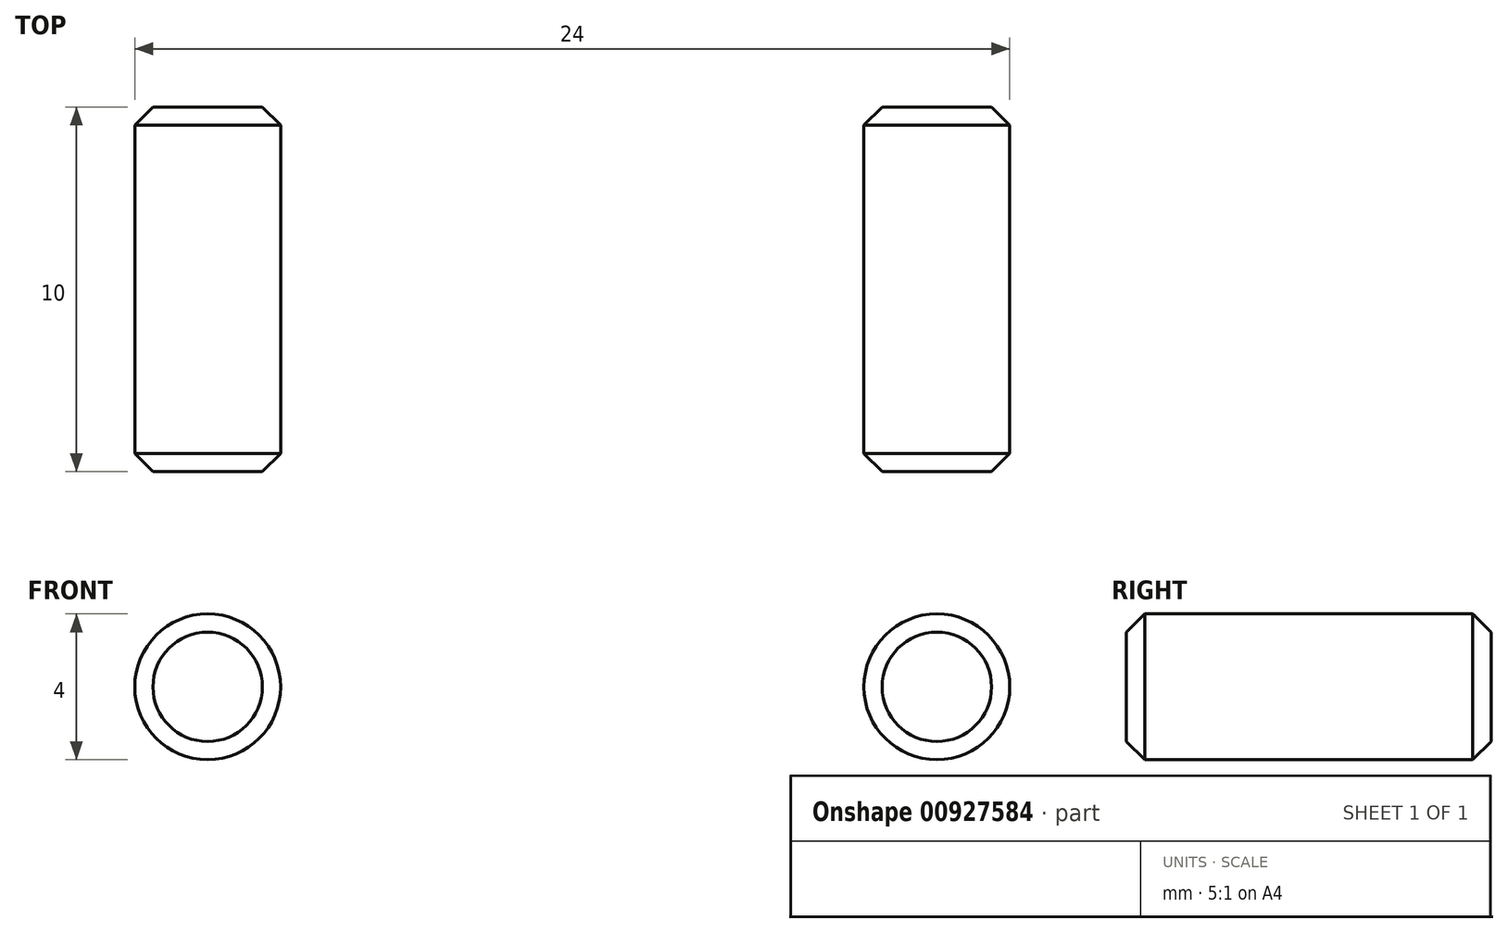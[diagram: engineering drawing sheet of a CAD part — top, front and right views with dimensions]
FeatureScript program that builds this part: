
annotation { "Feature Type Name" : "Feature", "Feature Type Description" : "" }
export const myFeature = defineFeature(function(context is Context, id is Id, definition is map)
    precondition{}
    {
        {
            var Q0;
            Q0=qCreatedBy(makeId("Right.planeOp"),FACE);
            var sketch = newSketch(context, id + "F0", { "sketchPlane" : qUnion([Q0])});
            skLineSegment(sketch, "E0.bottom", {"start": v(0, 0) * mm, "end": v(10, 0) * mm});
            skLineSegment(sketch, "E0.top", {"start": v(0, 11) * mm, "end": v(10, 11) * mm});
            skLineSegment(sketch, "E0.left", {"start": v(0, 0) * mm, "end": v(0, 11) * mm});
            skLineSegment(sketch, "E0.right", {"start": v(10, 0) * mm, "end": v(10, 11) * mm});
            skSolve(sketch);
        }
        {
            var Q0;
            Q0 = qSketchRegion(id + "F0", true);
            extrude(context, id + "F1", {"entities" : qUnion([Q0]), "oppositeDirection" : true, "depth" : 300 * mm, "offsetDistance" : 25 * mm});
        }
        {
            var Q0;
            Q0=makeQuery(id+"F1.opExtrude","SWEPT_FACE",FACE,{"disambiguationData":[OSD([sQuery(id+"F0.wireOp",EDGE,"E0.left")])]});
            var sketch = newSketch(context, id + "F2", { "sketchPlane" : qUnion([Q0])});
            skLineSegment(sketch, "E1", {"start": v(-271.81, 8) * mm, "end": v(-24.71, 8) * mm, "construction": true});
            skLineSegment(sketch, "E2.0", {"start": v(-327.74, 6.5) * mm, "end": v(9.8, 6.5) * mm, "construction": true});
            skLineSegment(sketch, "E3", {"start": v(-20, 30.82) * mm, "end": v(-20, -13.65) * mm, "construction": true});
            skLineSegment(sketch, "E4", {"start": v(-22.36, 15.05) * mm, "end": v(-22.36, 4.54) * mm, "construction": true});
            skLineSegment(sketch, "E5", {"start": v(-24.71, 15.08) * mm, "end": v(-24.71, 4.94) * mm, "construction": true});
            skLineSegment(sketch, "E6", {"start": v(-22.86, 11) * mm, "end": v(-22.36, 11) * mm});
            skLineSegment(sketch, "E7.MirrorCS", {"start": v(-21.86, 11) * mm, "end": v(-22.36, 11) * mm});
            skLineSegment(sketch, "E8", {"start": v(-24.71, 8) * mm, "end": v(-24.21, 8) * mm});
            skLineSegment(sketch, "E9", {"start": v(-24.21, 8) * mm, "end": v(-22.86, 11) * mm});
            skLineSegment(sketch, "E10", {"start": v(-20.5, 8) * mm, "end": v(-20, 8) * mm});
            skLineSegment(sketch, "E11", {"start": v(-21.86, 11) * mm, "end": v(-20.5, 8) * mm});
            skLineSegment(sketch, "E12.1.0.0", {"start": v(-25.21, 8) * mm, "end": v(-24.71, 8) * mm});
            skLineSegment(sketch, "E12.1.0.1", {"start": v(-26.57, 11) * mm, "end": v(-25.21, 8) * mm});
            skLineSegment(sketch, "E12.1.0.2", {"start": v(-26.57, 11) * mm, "end": v(-27.07, 11) * mm});
            skLineSegment(sketch, "E12.1.0.3", {"start": v(-27.57, 11) * mm, "end": v(-27.07, 11) * mm});
            skLineSegment(sketch, "E12.1.0.4", {"start": v(-28.92, 8) * mm, "end": v(-27.57, 11) * mm});
            skLineSegment(sketch, "E12.1.0.5", {"start": v(-29.42, 8) * mm, "end": v(-28.92, 8) * mm});
            skLineSegment(sketch, "E12.2.0.0", {"start": v(-29.92, 8) * mm, "end": v(-29.42, 8) * mm});
            skLineSegment(sketch, "E12.2.0.1", {"start": v(-31.28, 11) * mm, "end": v(-29.92, 8) * mm});
            skLineSegment(sketch, "E12.2.0.2", {"start": v(-31.28, 11) * mm, "end": v(-31.78, 11) * mm});
            skLineSegment(sketch, "E12.2.0.3", {"start": v(-32.28, 11) * mm, "end": v(-31.78, 11) * mm});
            skLineSegment(sketch, "E12.2.0.4", {"start": v(-33.64, 8) * mm, "end": v(-32.28, 11) * mm});
            skLineSegment(sketch, "E12.2.0.5", {"start": v(-34.14, 8) * mm, "end": v(-33.64, 8) * mm});
            skLineSegment(sketch, "E12.3.0.0", {"start": v(-34.64, 8) * mm, "end": v(-34.14, 8) * mm});
            skLineSegment(sketch, "E12.3.0.1", {"start": v(-36, 11) * mm, "end": v(-34.64, 8) * mm});
            skLineSegment(sketch, "E12.3.0.2", {"start": v(-36, 11) * mm, "end": v(-36.5, 11) * mm});
            skLineSegment(sketch, "E12.3.0.3", {"start": v(-37, 11) * mm, "end": v(-36.5, 11) * mm});
            skLineSegment(sketch, "E12.3.0.4", {"start": v(-38.35, 8) * mm, "end": v(-37, 11) * mm});
            skLineSegment(sketch, "E12.3.0.5", {"start": v(-38.85, 8) * mm, "end": v(-38.35, 8) * mm});
            skLineSegment(sketch, "E12.4.0.0", {"start": v(-39.35, 8) * mm, "end": v(-38.85, 8) * mm});
            skLineSegment(sketch, "E12.4.0.1", {"start": v(-40.7, 11) * mm, "end": v(-39.35, 8) * mm});
            skLineSegment(sketch, "E12.4.0.2", {"start": v(-40.7, 11) * mm, "end": v(-41.2, 11) * mm});
            skLineSegment(sketch, "E12.4.0.3", {"start": v(-41.7, 11) * mm, "end": v(-41.2, 11) * mm});
            skLineSegment(sketch, "E12.4.0.4", {"start": v(-43.06, 8) * mm, "end": v(-41.7, 11) * mm});
            skLineSegment(sketch, "E12.4.0.5", {"start": v(-43.56, 8) * mm, "end": v(-43.06, 8) * mm});
            skLineSegment(sketch, "E12.5.0.0", {"start": v(-44.06, 8) * mm, "end": v(-43.56, 8) * mm});
            skLineSegment(sketch, "E12.5.0.1", {"start": v(-45.42, 11) * mm, "end": v(-44.06, 8) * mm});
            skLineSegment(sketch, "E12.5.0.2", {"start": v(-45.42, 11) * mm, "end": v(-45.92, 11) * mm});
            skLineSegment(sketch, "E12.5.0.3", {"start": v(-46.42, 11) * mm, "end": v(-45.92, 11) * mm});
            skLineSegment(sketch, "E12.5.0.4", {"start": v(-47.77, 8) * mm, "end": v(-46.42, 11) * mm});
            skLineSegment(sketch, "E12.5.0.5", {"start": v(-48.27, 8) * mm, "end": v(-47.77, 8) * mm});
            skLineSegment(sketch, "E12.6.0.0", {"start": v(-48.77, 8) * mm, "end": v(-48.27, 8) * mm});
            skLineSegment(sketch, "E12.6.0.1", {"start": v(-50.13, 11) * mm, "end": v(-48.77, 8) * mm});
            skLineSegment(sketch, "E12.6.0.2", {"start": v(-50.13, 11) * mm, "end": v(-50.63, 11) * mm});
            skLineSegment(sketch, "E12.6.0.3", {"start": v(-51.13, 11) * mm, "end": v(-50.63, 11) * mm});
            skLineSegment(sketch, "E12.6.0.4", {"start": v(-52.48, 8) * mm, "end": v(-51.13, 11) * mm});
            skLineSegment(sketch, "E12.6.0.5", {"start": v(-52.98, 8) * mm, "end": v(-52.48, 8) * mm});
            skLineSegment(sketch, "E12.7.0.0", {"start": v(-53.48, 8) * mm, "end": v(-52.98, 8) * mm});
            skLineSegment(sketch, "E12.7.0.1", {"start": v(-54.84, 11) * mm, "end": v(-53.48, 8) * mm});
            skLineSegment(sketch, "E12.7.0.2", {"start": v(-54.84, 11) * mm, "end": v(-55.34, 11) * mm});
            skLineSegment(sketch, "E12.7.0.3", {"start": v(-55.84, 11) * mm, "end": v(-55.34, 11) * mm});
            skLineSegment(sketch, "E12.7.0.4", {"start": v(-57.2, 8) * mm, "end": v(-55.84, 11) * mm});
            skLineSegment(sketch, "E12.7.0.5", {"start": v(-57.7, 8) * mm, "end": v(-57.2, 8) * mm});
            skLineSegment(sketch, "E12.8.0.0", {"start": v(-58.2, 8) * mm, "end": v(-57.7, 8) * mm});
            skLineSegment(sketch, "E12.8.0.1", {"start": v(-59.55, 11) * mm, "end": v(-58.2, 8) * mm});
            skLineSegment(sketch, "E12.8.0.2", {"start": v(-59.55, 11) * mm, "end": v(-60.05, 11) * mm});
            skLineSegment(sketch, "E12.8.0.3", {"start": v(-60.55, 11) * mm, "end": v(-60.05, 11) * mm});
            skLineSegment(sketch, "E12.8.0.4", {"start": v(-61.9, 8) * mm, "end": v(-60.55, 11) * mm});
            skLineSegment(sketch, "E12.8.0.5", {"start": v(-62.4, 8) * mm, "end": v(-61.9, 8) * mm});
            skLineSegment(sketch, "E12.9.0.0", {"start": v(-62.9, 8) * mm, "end": v(-62.4, 8) * mm});
            skLineSegment(sketch, "E12.9.0.1", {"start": v(-64.26, 11) * mm, "end": v(-62.9, 8) * mm});
            skLineSegment(sketch, "E12.9.0.2", {"start": v(-64.26, 11) * mm, "end": v(-64.76, 11) * mm});
            skLineSegment(sketch, "E12.9.0.3", {"start": v(-65.26, 11) * mm, "end": v(-64.76, 11) * mm});
            skLineSegment(sketch, "E12.9.0.4", {"start": v(-66.62, 8) * mm, "end": v(-65.26, 11) * mm});
            skLineSegment(sketch, "E12.9.0.5", {"start": v(-67.12, 8) * mm, "end": v(-66.62, 8) * mm});
            skLineSegment(sketch, "E12.10.0.0", {"start": v(-67.62, 8) * mm, "end": v(-67.12, 8) * mm});
            skLineSegment(sketch, "E12.10.0.1", {"start": v(-68.98, 11) * mm, "end": v(-67.62, 8) * mm});
            skLineSegment(sketch, "E12.10.0.2", {"start": v(-68.98, 11) * mm, "end": v(-69.48, 11) * mm});
            skLineSegment(sketch, "E12.10.0.3", {"start": v(-69.98, 11) * mm, "end": v(-69.48, 11) * mm});
            skLineSegment(sketch, "E12.10.0.4", {"start": v(-71.33, 8) * mm, "end": v(-69.98, 11) * mm});
            skLineSegment(sketch, "E12.10.0.5", {"start": v(-71.83, 8) * mm, "end": v(-71.33, 8) * mm});
            skLineSegment(sketch, "E12.11.0.0", {"start": v(-72.33, 8) * mm, "end": v(-71.83, 8) * mm});
            skLineSegment(sketch, "E12.11.0.1", {"start": v(-73.69, 11) * mm, "end": v(-72.33, 8) * mm});
            skLineSegment(sketch, "E12.11.0.2", {"start": v(-73.69, 11) * mm, "end": v(-74.19, 11) * mm});
            skLineSegment(sketch, "E12.11.0.3", {"start": v(-74.69, 11) * mm, "end": v(-74.19, 11) * mm});
            skLineSegment(sketch, "E12.11.0.4", {"start": v(-76.04, 8) * mm, "end": v(-74.69, 11) * mm});
            skLineSegment(sketch, "E12.11.0.5", {"start": v(-76.54, 8) * mm, "end": v(-76.04, 8) * mm});
            skLineSegment(sketch, "E12.12.0.0", {"start": v(-77.04, 8) * mm, "end": v(-76.54, 8) * mm});
            skLineSegment(sketch, "E12.12.0.1", {"start": v(-78.4, 11) * mm, "end": v(-77.04, 8) * mm});
            skLineSegment(sketch, "E12.12.0.2", {"start": v(-78.4, 11) * mm, "end": v(-78.9, 11) * mm});
            skLineSegment(sketch, "E12.12.0.3", {"start": v(-79.4, 11) * mm, "end": v(-78.9, 11) * mm});
            skLineSegment(sketch, "E12.12.0.4", {"start": v(-80.76, 8) * mm, "end": v(-79.4, 11) * mm});
            skLineSegment(sketch, "E12.12.0.5", {"start": v(-81.26, 8) * mm, "end": v(-80.76, 8) * mm});
            skLineSegment(sketch, "E12.13.0.0", {"start": v(-81.76, 8) * mm, "end": v(-81.26, 8) * mm});
            skLineSegment(sketch, "E12.13.0.1", {"start": v(-83.11, 11) * mm, "end": v(-81.76, 8) * mm});
            skLineSegment(sketch, "E12.13.0.2", {"start": v(-83.11, 11) * mm, "end": v(-83.61, 11) * mm});
            skLineSegment(sketch, "E12.13.0.3", {"start": v(-84.11, 11) * mm, "end": v(-83.61, 11) * mm});
            skLineSegment(sketch, "E12.13.0.4", {"start": v(-85.47, 8) * mm, "end": v(-84.11, 11) * mm});
            skLineSegment(sketch, "E12.13.0.5", {"start": v(-85.97, 8) * mm, "end": v(-85.47, 8) * mm});
            skLineSegment(sketch, "E12.14.0.0", {"start": v(-86.47, 8) * mm, "end": v(-85.97, 8) * mm});
            skLineSegment(sketch, "E12.14.0.1", {"start": v(-87.82, 11) * mm, "end": v(-86.47, 8) * mm});
            skLineSegment(sketch, "E12.14.0.2", {"start": v(-87.82, 11) * mm, "end": v(-88.32, 11) * mm});
            skLineSegment(sketch, "E12.14.0.3", {"start": v(-88.82, 11) * mm, "end": v(-88.32, 11) * mm});
            skLineSegment(sketch, "E12.14.0.4", {"start": v(-90.18, 8) * mm, "end": v(-88.82, 11) * mm});
            skLineSegment(sketch, "E12.14.0.5", {"start": v(-90.68, 8) * mm, "end": v(-90.18, 8) * mm});
            skLineSegment(sketch, "E12.15.0.0", {"start": v(-91.18, 8) * mm, "end": v(-90.68, 8) * mm});
            skLineSegment(sketch, "E12.15.0.1", {"start": v(-92.54, 11) * mm, "end": v(-91.18, 8) * mm});
            skLineSegment(sketch, "E12.15.0.2", {"start": v(-92.54, 11) * mm, "end": v(-93.04, 11) * mm});
            skLineSegment(sketch, "E12.15.0.3", {"start": v(-93.54, 11) * mm, "end": v(-93.04, 11) * mm});
            skLineSegment(sketch, "E12.15.0.4", {"start": v(-94.9, 8) * mm, "end": v(-93.54, 11) * mm});
            skLineSegment(sketch, "E12.15.0.5", {"start": v(-95.4, 8) * mm, "end": v(-94.9, 8) * mm});
            skLineSegment(sketch, "E12.16.0.0", {"start": v(-95.9, 8) * mm, "end": v(-95.4, 8) * mm});
            skLineSegment(sketch, "E12.16.0.1", {"start": v(-97.25, 11) * mm, "end": v(-95.9, 8) * mm});
            skLineSegment(sketch, "E12.16.0.2", {"start": v(-97.25, 11) * mm, "end": v(-97.75, 11) * mm});
            skLineSegment(sketch, "E12.16.0.3", {"start": v(-98.25, 11) * mm, "end": v(-97.75, 11) * mm});
            skLineSegment(sketch, "E12.16.0.4", {"start": v(-99.6, 8) * mm, "end": v(-98.25, 11) * mm});
            skLineSegment(sketch, "E12.16.0.5", {"start": v(-100.1, 8) * mm, "end": v(-99.6, 8) * mm});
            skLineSegment(sketch, "E12.17.0.0", {"start": v(-100.6, 8) * mm, "end": v(-100.1, 8) * mm});
            skLineSegment(sketch, "E12.17.0.1", {"start": v(-101.96, 11) * mm, "end": v(-100.6, 8) * mm});
            skLineSegment(sketch, "E12.17.0.2", {"start": v(-101.96, 11) * mm, "end": v(-102.46, 11) * mm});
            skLineSegment(sketch, "E12.17.0.3", {"start": v(-102.96, 11) * mm, "end": v(-102.46, 11) * mm});
            skLineSegment(sketch, "E12.17.0.4", {"start": v(-104.32, 8) * mm, "end": v(-102.96, 11) * mm});
            skLineSegment(sketch, "E12.17.0.5", {"start": v(-104.82, 8) * mm, "end": v(-104.32, 8) * mm});
            skLineSegment(sketch, "E12.18.0.0", {"start": v(-105.32, 8) * mm, "end": v(-104.82, 8) * mm});
            skLineSegment(sketch, "E12.18.0.1", {"start": v(-106.67, 11) * mm, "end": v(-105.32, 8) * mm});
            skLineSegment(sketch, "E12.18.0.2", {"start": v(-106.67, 11) * mm, "end": v(-107.17, 11) * mm});
            skLineSegment(sketch, "E12.18.0.3", {"start": v(-107.67, 11) * mm, "end": v(-107.17, 11) * mm});
            skLineSegment(sketch, "E12.18.0.4", {"start": v(-109.03, 8) * mm, "end": v(-107.67, 11) * mm});
            skLineSegment(sketch, "E12.18.0.5", {"start": v(-109.53, 8) * mm, "end": v(-109.03, 8) * mm});
            skLineSegment(sketch, "E12.19.0.0", {"start": v(-110.03, 8) * mm, "end": v(-109.53, 8) * mm});
            skLineSegment(sketch, "E12.19.0.1", {"start": v(-111.38, 11) * mm, "end": v(-110.03, 8) * mm});
            skLineSegment(sketch, "E12.19.0.2", {"start": v(-111.38, 11) * mm, "end": v(-111.88, 11) * mm});
            skLineSegment(sketch, "E12.19.0.3", {"start": v(-112.38, 11) * mm, "end": v(-111.88, 11) * mm});
            skLineSegment(sketch, "E12.19.0.4", {"start": v(-113.74, 8) * mm, "end": v(-112.38, 11) * mm});
            skLineSegment(sketch, "E12.19.0.5", {"start": v(-114.24, 8) * mm, "end": v(-113.74, 8) * mm});
            skLineSegment(sketch, "E12.20.0.0", {"start": v(-114.74, 8) * mm, "end": v(-114.24, 8) * mm});
            skLineSegment(sketch, "E12.20.0.1", {"start": v(-116.1, 11) * mm, "end": v(-114.74, 8) * mm});
            skLineSegment(sketch, "E12.20.0.2", {"start": v(-116.1, 11) * mm, "end": v(-116.6, 11) * mm});
            skLineSegment(sketch, "E12.20.0.3", {"start": v(-117.1, 11) * mm, "end": v(-116.6, 11) * mm});
            skLineSegment(sketch, "E12.20.0.4", {"start": v(-118.45, 8) * mm, "end": v(-117.1, 11) * mm});
            skLineSegment(sketch, "E12.20.0.5", {"start": v(-118.95, 8) * mm, "end": v(-118.45, 8) * mm});
            skLineSegment(sketch, "E12.21.0.0", {"start": v(-119.45, 8) * mm, "end": v(-118.95, 8) * mm});
            skLineSegment(sketch, "E12.21.0.1", {"start": v(-120.8, 11) * mm, "end": v(-119.45, 8) * mm});
            skLineSegment(sketch, "E12.21.0.2", {"start": v(-120.8, 11) * mm, "end": v(-121.3, 11) * mm});
            skLineSegment(sketch, "E12.21.0.3", {"start": v(-121.8, 11) * mm, "end": v(-121.3, 11) * mm});
            skLineSegment(sketch, "E12.21.0.4", {"start": v(-123.16, 8) * mm, "end": v(-121.8, 11) * mm});
            skLineSegment(sketch, "E12.21.0.5", {"start": v(-123.66, 8) * mm, "end": v(-123.16, 8) * mm});
            skLineSegment(sketch, "E12.22.0.0", {"start": v(-124.16, 8) * mm, "end": v(-123.66, 8) * mm});
            skLineSegment(sketch, "E12.22.0.1", {"start": v(-125.52, 11) * mm, "end": v(-124.16, 8) * mm});
            skLineSegment(sketch, "E12.22.0.2", {"start": v(-125.52, 11) * mm, "end": v(-126.02, 11) * mm});
            skLineSegment(sketch, "E12.22.0.3", {"start": v(-126.52, 11) * mm, "end": v(-126.02, 11) * mm});
            skLineSegment(sketch, "E12.22.0.4", {"start": v(-127.88, 8) * mm, "end": v(-126.52, 11) * mm});
            skLineSegment(sketch, "E12.22.0.5", {"start": v(-128.38, 8) * mm, "end": v(-127.88, 8) * mm});
            skLineSegment(sketch, "E12.23.0.0", {"start": v(-128.88, 8) * mm, "end": v(-128.38, 8) * mm});
            skLineSegment(sketch, "E12.23.0.1", {"start": v(-130.23, 11) * mm, "end": v(-128.88, 8) * mm});
            skLineSegment(sketch, "E12.23.0.2", {"start": v(-130.23, 11) * mm, "end": v(-130.73, 11) * mm});
            skLineSegment(sketch, "E12.23.0.3", {"start": v(-131.23, 11) * mm, "end": v(-130.73, 11) * mm});
            skLineSegment(sketch, "E12.23.0.4", {"start": v(-132.59, 8) * mm, "end": v(-131.23, 11) * mm});
            skLineSegment(sketch, "E12.23.0.5", {"start": v(-133.09, 8) * mm, "end": v(-132.59, 8) * mm});
            skLineSegment(sketch, "E12.24.0.0", {"start": v(-133.59, 8) * mm, "end": v(-133.09, 8) * mm});
            skLineSegment(sketch, "E12.24.0.1", {"start": v(-134.94, 11) * mm, "end": v(-133.59, 8) * mm});
            skLineSegment(sketch, "E12.24.0.2", {"start": v(-134.94, 11) * mm, "end": v(-135.44, 11) * mm});
            skLineSegment(sketch, "E12.24.0.3", {"start": v(-135.94, 11) * mm, "end": v(-135.44, 11) * mm});
            skLineSegment(sketch, "E12.24.0.4", {"start": v(-137.3, 8) * mm, "end": v(-135.94, 11) * mm});
            skLineSegment(sketch, "E12.24.0.5", {"start": v(-137.8, 8) * mm, "end": v(-137.3, 8) * mm});
            skLineSegment(sketch, "E12.25.0.0", {"start": v(-138.3, 8) * mm, "end": v(-137.8, 8) * mm});
            skLineSegment(sketch, "E12.25.0.1", {"start": v(-139.66, 11) * mm, "end": v(-138.3, 8) * mm});
            skLineSegment(sketch, "E12.25.0.2", {"start": v(-139.66, 11) * mm, "end": v(-140.16, 11) * mm});
            skLineSegment(sketch, "E12.25.0.3", {"start": v(-140.66, 11) * mm, "end": v(-140.16, 11) * mm});
            skLineSegment(sketch, "E12.25.0.4", {"start": v(-142.01, 8) * mm, "end": v(-140.66, 11) * mm});
            skLineSegment(sketch, "E12.25.0.5", {"start": v(-142.51, 8) * mm, "end": v(-142.01, 8) * mm});
            skLineSegment(sketch, "E12.26.0.0", {"start": v(-143.01, 8) * mm, "end": v(-142.51, 8) * mm});
            skLineSegment(sketch, "E12.26.0.1", {"start": v(-144.37, 11) * mm, "end": v(-143.01, 8) * mm});
            skLineSegment(sketch, "E12.26.0.2", {"start": v(-144.37, 11) * mm, "end": v(-144.87, 11) * mm});
            skLineSegment(sketch, "E12.26.0.3", {"start": v(-145.37, 11) * mm, "end": v(-144.87, 11) * mm});
            skLineSegment(sketch, "E12.26.0.4", {"start": v(-146.72, 8) * mm, "end": v(-145.37, 11) * mm});
            skLineSegment(sketch, "E12.26.0.5", {"start": v(-147.22, 8) * mm, "end": v(-146.72, 8) * mm});
            skLineSegment(sketch, "E12.27.0.0", {"start": v(-147.72, 8) * mm, "end": v(-147.22, 8) * mm});
            skLineSegment(sketch, "E12.27.0.1", {"start": v(-149.08, 11) * mm, "end": v(-147.72, 8) * mm});
            skLineSegment(sketch, "E12.27.0.2", {"start": v(-149.08, 11) * mm, "end": v(-149.58, 11) * mm});
            skLineSegment(sketch, "E12.27.0.3", {"start": v(-150.08, 11) * mm, "end": v(-149.58, 11) * mm});
            skLineSegment(sketch, "E12.27.0.4", {"start": v(-151.44, 8) * mm, "end": v(-150.08, 11) * mm});
            skLineSegment(sketch, "E12.27.0.5", {"start": v(-151.94, 8) * mm, "end": v(-151.44, 8) * mm});
            skLineSegment(sketch, "E12.28.0.0", {"start": v(-152.44, 8) * mm, "end": v(-151.94, 8) * mm});
            skLineSegment(sketch, "E12.28.0.1", {"start": v(-153.8, 11) * mm, "end": v(-152.44, 8) * mm});
            skLineSegment(sketch, "E12.28.0.2", {"start": v(-153.8, 11) * mm, "end": v(-154.3, 11) * mm});
            skLineSegment(sketch, "E12.28.0.3", {"start": v(-154.8, 11) * mm, "end": v(-154.3, 11) * mm});
            skLineSegment(sketch, "E12.28.0.4", {"start": v(-156.15, 8) * mm, "end": v(-154.8, 11) * mm});
            skLineSegment(sketch, "E12.28.0.5", {"start": v(-156.65, 8) * mm, "end": v(-156.15, 8) * mm});
            skLineSegment(sketch, "E12.29.0.0", {"start": v(-157.15, 8) * mm, "end": v(-156.65, 8) * mm});
            skLineSegment(sketch, "E12.29.0.1", {"start": v(-158.5, 11) * mm, "end": v(-157.15, 8) * mm});
            skLineSegment(sketch, "E12.29.0.2", {"start": v(-158.5, 11) * mm, "end": v(-159, 11) * mm});
            skLineSegment(sketch, "E12.29.0.3", {"start": v(-159.5, 11) * mm, "end": v(-159, 11) * mm});
            skLineSegment(sketch, "E12.29.0.4", {"start": v(-160.86, 8) * mm, "end": v(-159.5, 11) * mm});
            skLineSegment(sketch, "E12.29.0.5", {"start": v(-161.36, 8) * mm, "end": v(-160.86, 8) * mm});
            skLineSegment(sketch, "E12.30.0.0", {"start": v(-161.86, 8) * mm, "end": v(-161.36, 8) * mm});
            skLineSegment(sketch, "E12.30.0.1", {"start": v(-163.22, 11) * mm, "end": v(-161.86, 8) * mm});
            skLineSegment(sketch, "E12.30.0.2", {"start": v(-163.22, 11) * mm, "end": v(-163.72, 11) * mm});
            skLineSegment(sketch, "E12.30.0.3", {"start": v(-164.22, 11) * mm, "end": v(-163.72, 11) * mm});
            skLineSegment(sketch, "E12.30.0.4", {"start": v(-165.57, 8) * mm, "end": v(-164.22, 11) * mm});
            skLineSegment(sketch, "E12.30.0.5", {"start": v(-166.07, 8) * mm, "end": v(-165.57, 8) * mm});
            skLineSegment(sketch, "E12.31.0.0", {"start": v(-166.57, 8) * mm, "end": v(-166.07, 8) * mm});
            skLineSegment(sketch, "E12.31.0.1", {"start": v(-167.93, 11) * mm, "end": v(-166.57, 8) * mm});
            skLineSegment(sketch, "E12.31.0.2", {"start": v(-167.93, 11) * mm, "end": v(-168.43, 11) * mm});
            skLineSegment(sketch, "E12.31.0.3", {"start": v(-168.93, 11) * mm, "end": v(-168.43, 11) * mm});
            skLineSegment(sketch, "E12.31.0.4", {"start": v(-170.28, 8) * mm, "end": v(-168.93, 11) * mm});
            skLineSegment(sketch, "E12.31.0.5", {"start": v(-170.78, 8) * mm, "end": v(-170.28, 8) * mm});
            skLineSegment(sketch, "E12.32.0.0", {"start": v(-171.28, 8) * mm, "end": v(-170.78, 8) * mm});
            skLineSegment(sketch, "E12.32.0.1", {"start": v(-172.64, 11) * mm, "end": v(-171.28, 8) * mm});
            skLineSegment(sketch, "E12.32.0.2", {"start": v(-172.64, 11) * mm, "end": v(-173.14, 11) * mm});
            skLineSegment(sketch, "E12.32.0.3", {"start": v(-173.64, 11) * mm, "end": v(-173.14, 11) * mm});
            skLineSegment(sketch, "E12.32.0.4", {"start": v(-175, 8) * mm, "end": v(-173.64, 11) * mm});
            skLineSegment(sketch, "E12.32.0.5", {"start": v(-175.5, 8) * mm, "end": v(-175, 8) * mm});
            skLineSegment(sketch, "E12.33.0.0", {"start": v(-176, 8) * mm, "end": v(-175.5, 8) * mm});
            skLineSegment(sketch, "E12.33.0.1", {"start": v(-177.35, 11) * mm, "end": v(-176, 8) * mm});
            skLineSegment(sketch, "E12.33.0.2", {"start": v(-177.35, 11) * mm, "end": v(-177.85, 11) * mm});
            skLineSegment(sketch, "E12.33.0.3", {"start": v(-178.35, 11) * mm, "end": v(-177.85, 11) * mm});
            skLineSegment(sketch, "E12.33.0.4", {"start": v(-179.7, 8) * mm, "end": v(-178.35, 11) * mm});
            skLineSegment(sketch, "E12.33.0.5", {"start": v(-180.2, 8) * mm, "end": v(-179.7, 8) * mm});
            skLineSegment(sketch, "E12.34.0.0", {"start": v(-180.7, 8) * mm, "end": v(-180.2, 8) * mm});
            skLineSegment(sketch, "E12.34.0.1", {"start": v(-182.06, 11) * mm, "end": v(-180.7, 8) * mm});
            skLineSegment(sketch, "E12.34.0.2", {"start": v(-182.06, 11) * mm, "end": v(-182.56, 11) * mm});
            skLineSegment(sketch, "E12.34.0.3", {"start": v(-183.06, 11) * mm, "end": v(-182.56, 11) * mm});
            skLineSegment(sketch, "E12.34.0.4", {"start": v(-184.42, 8) * mm, "end": v(-183.06, 11) * mm});
            skLineSegment(sketch, "E12.34.0.5", {"start": v(-184.92, 8) * mm, "end": v(-184.42, 8) * mm});
            skLineSegment(sketch, "E12.35.0.0", {"start": v(-185.42, 8) * mm, "end": v(-184.92, 8) * mm});
            skLineSegment(sketch, "E12.35.0.1", {"start": v(-186.78, 11) * mm, "end": v(-185.42, 8) * mm});
            skLineSegment(sketch, "E12.35.0.2", {"start": v(-186.78, 11) * mm, "end": v(-187.28, 11) * mm});
            skLineSegment(sketch, "E12.35.0.3", {"start": v(-187.78, 11) * mm, "end": v(-187.28, 11) * mm});
            skLineSegment(sketch, "E12.35.0.4", {"start": v(-189.13, 8) * mm, "end": v(-187.78, 11) * mm});
            skLineSegment(sketch, "E12.35.0.5", {"start": v(-189.63, 8) * mm, "end": v(-189.13, 8) * mm});
            skLineSegment(sketch, "E12.36.0.0", {"start": v(-190.13, 8) * mm, "end": v(-189.63, 8) * mm});
            skLineSegment(sketch, "E12.36.0.1", {"start": v(-191.49, 11) * mm, "end": v(-190.13, 8) * mm});
            skLineSegment(sketch, "E12.36.0.2", {"start": v(-191.49, 11) * mm, "end": v(-191.99, 11) * mm});
            skLineSegment(sketch, "E12.36.0.3", {"start": v(-192.49, 11) * mm, "end": v(-191.99, 11) * mm});
            skLineSegment(sketch, "E12.36.0.4", {"start": v(-193.84, 8) * mm, "end": v(-192.49, 11) * mm});
            skLineSegment(sketch, "E12.36.0.5", {"start": v(-194.34, 8) * mm, "end": v(-193.84, 8) * mm});
            skLineSegment(sketch, "E12.37.0.0", {"start": v(-194.84, 8) * mm, "end": v(-194.34, 8) * mm});
            skLineSegment(sketch, "E12.37.0.1", {"start": v(-196.2, 11) * mm, "end": v(-194.84, 8) * mm});
            skLineSegment(sketch, "E12.37.0.2", {"start": v(-196.2, 11) * mm, "end": v(-196.7, 11) * mm});
            skLineSegment(sketch, "E12.37.0.3", {"start": v(-197.2, 11) * mm, "end": v(-196.7, 11) * mm});
            skLineSegment(sketch, "E12.37.0.4", {"start": v(-198.56, 8) * mm, "end": v(-197.2, 11) * mm});
            skLineSegment(sketch, "E12.37.0.5", {"start": v(-199.06, 8) * mm, "end": v(-198.56, 8) * mm});
            skLineSegment(sketch, "E12.38.0.0", {"start": v(-199.56, 8) * mm, "end": v(-199.06, 8) * mm});
            skLineSegment(sketch, "E12.38.0.1", {"start": v(-200.91, 11) * mm, "end": v(-199.56, 8) * mm});
            skLineSegment(sketch, "E12.38.0.2", {"start": v(-200.91, 11) * mm, "end": v(-201.41, 11) * mm});
            skLineSegment(sketch, "E12.38.0.3", {"start": v(-201.91, 11) * mm, "end": v(-201.41, 11) * mm});
            skLineSegment(sketch, "E12.38.0.4", {"start": v(-203.27, 8) * mm, "end": v(-201.91, 11) * mm});
            skLineSegment(sketch, "E12.38.0.5", {"start": v(-203.77, 8) * mm, "end": v(-203.27, 8) * mm});
            skLineSegment(sketch, "E12.39.0.0", {"start": v(-204.27, 8) * mm, "end": v(-203.77, 8) * mm});
            skLineSegment(sketch, "E12.39.0.1", {"start": v(-205.62, 11) * mm, "end": v(-204.27, 8) * mm});
            skLineSegment(sketch, "E12.39.0.2", {"start": v(-205.62, 11) * mm, "end": v(-206.12, 11) * mm});
            skLineSegment(sketch, "E12.39.0.3", {"start": v(-206.62, 11) * mm, "end": v(-206.12, 11) * mm});
            skLineSegment(sketch, "E12.39.0.4", {"start": v(-207.98, 8) * mm, "end": v(-206.62, 11) * mm});
            skLineSegment(sketch, "E12.39.0.5", {"start": v(-208.48, 8) * mm, "end": v(-207.98, 8) * mm});
            skLineSegment(sketch, "E12.40.0.0", {"start": v(-208.98, 8) * mm, "end": v(-208.48, 8) * mm});
            skLineSegment(sketch, "E12.40.0.1", {"start": v(-210.34, 11) * mm, "end": v(-208.98, 8) * mm});
            skLineSegment(sketch, "E12.40.0.2", {"start": v(-210.34, 11) * mm, "end": v(-210.84, 11) * mm});
            skLineSegment(sketch, "E12.40.0.3", {"start": v(-211.34, 11) * mm, "end": v(-210.84, 11) * mm});
            skLineSegment(sketch, "E12.40.0.4", {"start": v(-212.7, 8) * mm, "end": v(-211.34, 11) * mm});
            skLineSegment(sketch, "E12.40.0.5", {"start": v(-213.2, 8) * mm, "end": v(-212.7, 8) * mm});
            skLineSegment(sketch, "E12.41.0.0", {"start": v(-213.7, 8) * mm, "end": v(-213.2, 8) * mm});
            skLineSegment(sketch, "E12.41.0.1", {"start": v(-215.05, 11) * mm, "end": v(-213.7, 8) * mm});
            skLineSegment(sketch, "E12.41.0.2", {"start": v(-215.05, 11) * mm, "end": v(-215.55, 11) * mm});
            skLineSegment(sketch, "E12.41.0.3", {"start": v(-216.05, 11) * mm, "end": v(-215.55, 11) * mm});
            skLineSegment(sketch, "E12.41.0.4", {"start": v(-217.4, 8) * mm, "end": v(-216.05, 11) * mm});
            skLineSegment(sketch, "E12.41.0.5", {"start": v(-217.9, 8) * mm, "end": v(-217.4, 8) * mm});
            skLineSegment(sketch, "E12.42.0.0", {"start": v(-218.4, 8) * mm, "end": v(-217.9, 8) * mm});
            skLineSegment(sketch, "E12.42.0.1", {"start": v(-219.76, 11) * mm, "end": v(-218.4, 8) * mm});
            skLineSegment(sketch, "E12.42.0.2", {"start": v(-219.76, 11) * mm, "end": v(-220.26, 11) * mm});
            skLineSegment(sketch, "E12.42.0.3", {"start": v(-220.76, 11) * mm, "end": v(-220.26, 11) * mm});
            skLineSegment(sketch, "E12.42.0.4", {"start": v(-222.12, 8) * mm, "end": v(-220.76, 11) * mm});
            skLineSegment(sketch, "E12.42.0.5", {"start": v(-222.62, 8) * mm, "end": v(-222.12, 8) * mm});
            skLineSegment(sketch, "E12.43.0.0", {"start": v(-223.12, 8) * mm, "end": v(-222.62, 8) * mm});
            skLineSegment(sketch, "E12.43.0.1", {"start": v(-224.47, 11) * mm, "end": v(-223.12, 8) * mm});
            skLineSegment(sketch, "E12.43.0.2", {"start": v(-224.47, 11) * mm, "end": v(-224.97, 11) * mm});
            skLineSegment(sketch, "E12.43.0.3", {"start": v(-225.47, 11) * mm, "end": v(-224.97, 11) * mm});
            skLineSegment(sketch, "E12.43.0.4", {"start": v(-226.83, 8) * mm, "end": v(-225.47, 11) * mm});
            skLineSegment(sketch, "E12.43.0.5", {"start": v(-227.33, 8) * mm, "end": v(-226.83, 8) * mm});
            skLineSegment(sketch, "E12.44.0.0", {"start": v(-227.83, 8) * mm, "end": v(-227.33, 8) * mm});
            skLineSegment(sketch, "E12.44.0.1", {"start": v(-229.18, 11) * mm, "end": v(-227.83, 8) * mm});
            skLineSegment(sketch, "E12.44.0.2", {"start": v(-229.18, 11) * mm, "end": v(-229.68, 11) * mm});
            skLineSegment(sketch, "E12.44.0.3", {"start": v(-230.18, 11) * mm, "end": v(-229.68, 11) * mm});
            skLineSegment(sketch, "E12.44.0.4", {"start": v(-231.54, 8) * mm, "end": v(-230.18, 11) * mm});
            skLineSegment(sketch, "E12.44.0.5", {"start": v(-232.04, 8) * mm, "end": v(-231.54, 8) * mm});
            skLineSegment(sketch, "E12.45.0.0", {"start": v(-232.54, 8) * mm, "end": v(-232.04, 8) * mm});
            skLineSegment(sketch, "E12.45.0.1", {"start": v(-233.9, 11) * mm, "end": v(-232.54, 8) * mm});
            skLineSegment(sketch, "E12.45.0.2", {"start": v(-233.9, 11) * mm, "end": v(-234.4, 11) * mm});
            skLineSegment(sketch, "E12.45.0.3", {"start": v(-234.9, 11) * mm, "end": v(-234.4, 11) * mm});
            skLineSegment(sketch, "E12.45.0.4", {"start": v(-236.25, 8) * mm, "end": v(-234.9, 11) * mm});
            skLineSegment(sketch, "E12.45.0.5", {"start": v(-236.75, 8) * mm, "end": v(-236.25, 8) * mm});
            skLineSegment(sketch, "E12.46.0.0", {"start": v(-237.25, 8) * mm, "end": v(-236.75, 8) * mm});
            skLineSegment(sketch, "E12.46.0.1", {"start": v(-238.6, 11) * mm, "end": v(-237.25, 8) * mm});
            skLineSegment(sketch, "E12.46.0.2", {"start": v(-238.6, 11) * mm, "end": v(-239.1, 11) * mm});
            skLineSegment(sketch, "E12.46.0.3", {"start": v(-239.6, 11) * mm, "end": v(-239.1, 11) * mm});
            skLineSegment(sketch, "E12.46.0.4", {"start": v(-240.96, 8) * mm, "end": v(-239.6, 11) * mm});
            skLineSegment(sketch, "E12.46.0.5", {"start": v(-241.46, 8) * mm, "end": v(-240.96, 8) * mm});
            skLineSegment(sketch, "E12.47.0.0", {"start": v(-241.96, 8) * mm, "end": v(-241.46, 8) * mm});
            skLineSegment(sketch, "E12.47.0.1", {"start": v(-243.32, 11) * mm, "end": v(-241.96, 8) * mm});
            skLineSegment(sketch, "E12.47.0.2", {"start": v(-243.32, 11) * mm, "end": v(-243.82, 11) * mm});
            skLineSegment(sketch, "E12.47.0.3", {"start": v(-244.32, 11) * mm, "end": v(-243.82, 11) * mm});
            skLineSegment(sketch, "E12.47.0.4", {"start": v(-245.68, 8) * mm, "end": v(-244.32, 11) * mm});
            skLineSegment(sketch, "E12.47.0.5", {"start": v(-246.18, 8) * mm, "end": v(-245.68, 8) * mm});
            skLineSegment(sketch, "E12.48.0.0", {"start": v(-246.68, 8) * mm, "end": v(-246.18, 8) * mm});
            skLineSegment(sketch, "E12.48.0.1", {"start": v(-248.03, 11) * mm, "end": v(-246.68, 8) * mm});
            skLineSegment(sketch, "E12.48.0.2", {"start": v(-248.03, 11) * mm, "end": v(-248.53, 11) * mm});
            skLineSegment(sketch, "E12.48.0.3", {"start": v(-249.03, 11) * mm, "end": v(-248.53, 11) * mm});
            skLineSegment(sketch, "E12.48.0.4", {"start": v(-250.39, 8) * mm, "end": v(-249.03, 11) * mm});
            skLineSegment(sketch, "E12.48.0.5", {"start": v(-250.89, 8) * mm, "end": v(-250.39, 8) * mm});
            skLineSegment(sketch, "E12.49.0.0", {"start": v(-251.39, 8) * mm, "end": v(-250.89, 8) * mm});
            skLineSegment(sketch, "E12.49.0.1", {"start": v(-252.74, 11) * mm, "end": v(-251.39, 8) * mm});
            skLineSegment(sketch, "E12.49.0.2", {"start": v(-252.74, 11) * mm, "end": v(-253.24, 11) * mm});
            skLineSegment(sketch, "E12.49.0.3", {"start": v(-253.74, 11) * mm, "end": v(-253.24, 11) * mm});
            skLineSegment(sketch, "E12.49.0.4", {"start": v(-255.1, 8) * mm, "end": v(-253.74, 11) * mm});
            skLineSegment(sketch, "E12.49.0.5", {"start": v(-255.6, 8) * mm, "end": v(-255.1, 8) * mm});
            skLineSegment(sketch, "E12.50.0.0", {"start": v(-256.1, 8) * mm, "end": v(-255.6, 8) * mm});
            skLineSegment(sketch, "E12.50.0.1", {"start": v(-257.46, 11) * mm, "end": v(-256.1, 8) * mm});
            skLineSegment(sketch, "E12.50.0.2", {"start": v(-257.46, 11) * mm, "end": v(-257.96, 11) * mm});
            skLineSegment(sketch, "E12.50.0.3", {"start": v(-258.46, 11) * mm, "end": v(-257.96, 11) * mm});
            skLineSegment(sketch, "E12.50.0.4", {"start": v(-259.81, 8) * mm, "end": v(-258.46, 11) * mm});
            skLineSegment(sketch, "E12.50.0.5", {"start": v(-260.31, 8) * mm, "end": v(-259.81, 8) * mm});
            skLineSegment(sketch, "E12.51.0.0", {"start": v(-260.81, 8) * mm, "end": v(-260.31, 8) * mm});
            skLineSegment(sketch, "E12.51.0.1", {"start": v(-262.17, 11) * mm, "end": v(-260.81, 8) * mm});
            skLineSegment(sketch, "E12.51.0.2", {"start": v(-262.17, 11) * mm, "end": v(-262.67, 11) * mm});
            skLineSegment(sketch, "E12.51.0.3", {"start": v(-263.17, 11) * mm, "end": v(-262.67, 11) * mm});
            skLineSegment(sketch, "E12.51.0.4", {"start": v(-264.52, 8) * mm, "end": v(-263.17, 11) * mm});
            skLineSegment(sketch, "E12.51.0.5", {"start": v(-265.02, 8) * mm, "end": v(-264.52, 8) * mm});
            skLineSegment(sketch, "E12.52.0.0", {"start": v(-265.52, 8) * mm, "end": v(-265.02, 8) * mm});
            skLineSegment(sketch, "E12.52.0.1", {"start": v(-266.88, 11) * mm, "end": v(-265.52, 8) * mm});
            skLineSegment(sketch, "E12.52.0.2", {"start": v(-266.88, 11) * mm, "end": v(-267.38, 11) * mm});
            skLineSegment(sketch, "E12.52.0.3", {"start": v(-267.88, 11) * mm, "end": v(-267.38, 11) * mm});
            skLineSegment(sketch, "E12.52.0.4", {"start": v(-269.24, 8) * mm, "end": v(-267.88, 11) * mm});
            skLineSegment(sketch, "E12.52.0.5", {"start": v(-269.74, 8) * mm, "end": v(-269.24, 8) * mm});
            skLineSegment(sketch, "E12.53.0.0", {"start": v(-270.24, 8) * mm, "end": v(-269.74, 8) * mm});
            skLineSegment(sketch, "E12.53.0.1", {"start": v(-271.6, 11) * mm, "end": v(-270.24, 8) * mm});
            skLineSegment(sketch, "E12.53.0.2", {"start": v(-271.6, 11) * mm, "end": v(-272.1, 11) * mm});
            skLineSegment(sketch, "E12.53.0.3", {"start": v(-272.6, 11) * mm, "end": v(-272.1, 11) * mm});
            skLineSegment(sketch, "E12.53.0.4", {"start": v(-273.95, 8) * mm, "end": v(-272.6, 11) * mm});
            skLineSegment(sketch, "E12.53.0.5", {"start": v(-274.45, 8) * mm, "end": v(-273.95, 8) * mm});
            skLineSegment(sketch, "E12.54.0.0", {"start": v(-274.95, 8) * mm, "end": v(-274.45, 8) * mm});
            skLineSegment(sketch, "E12.54.0.1", {"start": v(-276.3, 11) * mm, "end": v(-274.95, 8) * mm});
            skLineSegment(sketch, "E12.54.0.2", {"start": v(-276.3, 11) * mm, "end": v(-276.8, 11) * mm});
            skLineSegment(sketch, "E12.54.0.3", {"start": v(-277.3, 11) * mm, "end": v(-276.8, 11) * mm});
            skLineSegment(sketch, "E12.54.0.4", {"start": v(-278.66, 8) * mm, "end": v(-277.3, 11) * mm});
            skLineSegment(sketch, "E12.54.0.5", {"start": v(-279.16, 8) * mm, "end": v(-278.66, 8) * mm});
            skLineSegment(sketch, "E12.direction1", {"start": v(-20.5, 8) * mm, "end": v(-22.36, 8) * mm, "construction": true});
            skLineSegment(sketch, "E13", {"start": v(-20, 8) * mm, "end": v(-20, 11) * mm});
            skLineSegment(sketch, "E14", {"start": v(-20, 11) * mm, "end": v(-300, 11) * mm});
            skLineSegment(sketch, "E15", {"start": v(-279.16, 15.08) * mm, "end": v(-279.16, 3.6) * mm, "construction": true});
            skLineSegment(sketch, "E16.1.0.0", {"start": v(-279.66, 8) * mm, "end": v(-279.16, 8) * mm});
            skLineSegment(sketch, "E16.1.0.1", {"start": v(-281.02, 11) * mm, "end": v(-279.66, 8) * mm});
            skLineSegment(sketch, "E16.1.0.2", {"start": v(-281.02, 11) * mm, "end": v(-281.52, 11) * mm});
            skLineSegment(sketch, "E16.1.0.3", {"start": v(-282.02, 11) * mm, "end": v(-281.52, 11) * mm});
            skLineSegment(sketch, "E16.1.0.4", {"start": v(-283.37, 8) * mm, "end": v(-282.02, 11) * mm});
            skLineSegment(sketch, "E16.1.0.5", {"start": v(-283.87, 8) * mm, "end": v(-283.37, 8) * mm});
            skLineSegment(sketch, "E16.2.0.0", {"start": v(-284.37, 8) * mm, "end": v(-283.87, 8) * mm});
            skLineSegment(sketch, "E16.2.0.1", {"start": v(-285.73, 11) * mm, "end": v(-284.37, 8) * mm});
            skLineSegment(sketch, "E16.2.0.2", {"start": v(-285.73, 11) * mm, "end": v(-286.23, 11) * mm});
            skLineSegment(sketch, "E16.2.0.3", {"start": v(-286.73, 11) * mm, "end": v(-286.23, 11) * mm});
            skLineSegment(sketch, "E16.2.0.4", {"start": v(-288.08, 8) * mm, "end": v(-286.73, 11) * mm});
            skLineSegment(sketch, "E16.2.0.5", {"start": v(-288.58, 8) * mm, "end": v(-288.08, 8) * mm});
            skLineSegment(sketch, "E16.3.0.0", {"start": v(-289.08, 8) * mm, "end": v(-288.58, 8) * mm});
            skLineSegment(sketch, "E16.3.0.1", {"start": v(-290.44, 11) * mm, "end": v(-289.08, 8) * mm});
            skLineSegment(sketch, "E16.3.0.2", {"start": v(-290.44, 11) * mm, "end": v(-290.94, 11) * mm});
            skLineSegment(sketch, "E16.3.0.3", {"start": v(-291.44, 11) * mm, "end": v(-290.94, 11) * mm});
            skLineSegment(sketch, "E16.3.0.4", {"start": v(-292.8, 8) * mm, "end": v(-291.44, 11) * mm});
            skLineSegment(sketch, "E16.3.0.5", {"start": v(-293.3, 8) * mm, "end": v(-292.8, 8) * mm});
            skLineSegment(sketch, "E16.4.0.0", {"start": v(-293.8, 8) * mm, "end": v(-293.3, 8) * mm});
            skLineSegment(sketch, "E16.4.0.1", {"start": v(-295.15, 11) * mm, "end": v(-293.8, 8) * mm});
            skLineSegment(sketch, "E16.4.0.2", {"start": v(-295.15, 11) * mm, "end": v(-295.65, 11) * mm});
            skLineSegment(sketch, "E16.4.0.3", {"start": v(-296.15, 11) * mm, "end": v(-295.65, 11) * mm});
            skLineSegment(sketch, "E16.4.0.4", {"start": v(-297.5, 8) * mm, "end": v(-296.15, 11) * mm});
            skLineSegment(sketch, "E16.4.0.5", {"start": v(-298, 8) * mm, "end": v(-297.5, 8) * mm});
            skLineSegment(sketch, "E16.direction1", {"start": v(-274.95, 8) * mm, "end": v(-279.66, 8) * mm, "construction": true});
            skLineSegment(sketch, "E17", {"start": v(-298, 8) * mm, "end": v(-300, 8) * mm});
            skLineSegment(sketch, "E18.trimOffspring", {"start": v(-24.21, 8) * mm, "end": v(-25.21, 8) * mm});
            skLineSegment(sketch, "E19.1.0.0", {"start": v(-15.79, 8) * mm, "end": v(-15.29, 8) * mm});
            skLineSegment(sketch, "E19.1.0.1", {"start": v(-17.14, 11) * mm, "end": v(-15.79, 8) * mm});
            skLineSegment(sketch, "E19.1.0.2", {"start": v(-17.14, 11) * mm, "end": v(-17.64, 11) * mm});
            skLineSegment(sketch, "E19.1.0.3", {"start": v(-18.14, 11) * mm, "end": v(-17.64, 11) * mm});
            skLineSegment(sketch, "E19.1.0.4", {"start": v(-19.5, 8) * mm, "end": v(-18.14, 11) * mm});
            skLineSegment(sketch, "E19.1.0.5", {"start": v(-20, 8) * mm, "end": v(-19.5, 8) * mm});
            skLineSegment(sketch, "E19.2.0.0", {"start": v(-11.08, 8) * mm, "end": v(-10.58, 8) * mm});
            skLineSegment(sketch, "E19.2.0.1", {"start": v(-12.43, 11) * mm, "end": v(-11.08, 8) * mm});
            skLineSegment(sketch, "E19.2.0.2", {"start": v(-12.43, 11) * mm, "end": v(-12.93, 11) * mm});
            skLineSegment(sketch, "E19.2.0.3", {"start": v(-13.43, 11) * mm, "end": v(-12.93, 11) * mm});
            skLineSegment(sketch, "E19.2.0.4", {"start": v(-14.79, 8) * mm, "end": v(-13.43, 11) * mm});
            skLineSegment(sketch, "E19.2.0.5", {"start": v(-15.29, 8) * mm, "end": v(-14.79, 8) * mm});
            skLineSegment(sketch, "E19.3.0.0", {"start": v(-6.36, 8) * mm, "end": v(-5.86, 8) * mm});
            skLineSegment(sketch, "E19.3.0.1", {"start": v(-7.72, 11) * mm, "end": v(-6.36, 8) * mm});
            skLineSegment(sketch, "E19.3.0.2", {"start": v(-7.72, 11) * mm, "end": v(-8.22, 11) * mm});
            skLineSegment(sketch, "E19.3.0.3", {"start": v(-8.72, 11) * mm, "end": v(-8.22, 11) * mm});
            skLineSegment(sketch, "E19.3.0.4", {"start": v(-10.08, 8) * mm, "end": v(-8.72, 11) * mm});
            skLineSegment(sketch, "E19.3.0.5", {"start": v(-10.58, 8) * mm, "end": v(-10.08, 8) * mm});
            skLineSegment(sketch, "E19.4.0.0", {"start": v(-1.65, 8) * mm, "end": v(-1.15, 8) * mm});
            skLineSegment(sketch, "E19.4.0.1", {"start": v(-3, 11) * mm, "end": v(-1.65, 8) * mm});
            skLineSegment(sketch, "E19.4.0.2", {"start": v(-3, 11) * mm, "end": v(-3.5, 11) * mm});
            skLineSegment(sketch, "E19.4.0.3", {"start": v(-4, 11) * mm, "end": v(-3.5, 11) * mm});
            skLineSegment(sketch, "E19.4.0.4", {"start": v(-5.36, 8) * mm, "end": v(-4, 11) * mm});
            skLineSegment(sketch, "E19.4.0.5", {"start": v(-5.86, 8) * mm, "end": v(-5.36, 8) * mm});
            skLineSegment(sketch, "E19.direction1", {"start": v(-20.5, 8) * mm, "end": v(-15.79, 8) * mm, "construction": true});
            skLineSegment(sketch, "E20", {"start": v(-20, 8) * mm, "end": v(-302.1, 8) * mm, "construction": true});
            skLineSegment(sketch, "E21", {"start": v(-1.15, 8) * mm, "end": v(0, 8) * mm});
            skLineSegment(sketch, "E22", {"start": v(0, 8) * mm, "end": v(0, 11) * mm});
            skLineSegment(sketch, "E23", {"start": v(0, 11) * mm, "end": v(-20, 11) * mm});
            skLineSegment(sketch, "E24", {"start": v(-300, 11) * mm, "end": v(-300, 8) * mm});
            skSolve(sketch);
        }
        {
            var Q0;
            Q0 = qSketchRegion(id + "F2", true);
            extrude(context, id + "F3", {"entities" : qUnion([Q0]), "operationType" : NewBodyOperationType.REMOVE, "endBound" : BoundingType.THROUGH_ALL, "oppositeDirection" : true, "depth" : 25 * mm, "offsetDistance" : 25 * mm});
        }
        {
            var Q0;
            Q0=makeQuery(id+"F1.opExtrude","SWEPT_FACE",FACE,{"disambiguationData":[OSD([sQuery(id+"F0.wireOp",EDGE,"E0.right")])]});
            var sketch = newSketch(context, id + "F4", { "sketchPlane" : qUnion([Q0])});
            skLineSegment(sketch, "E25", {"start": v(-24.19, 4) * mm, "end": v(352.02, 4) * mm, "construction": true});
            skLineSegment(sketch, "E26", {"start": v(20, 22.41) * mm, "end": v(20, -14.74) * mm, "construction": true});
            skCircle(sketch, "E27", {"center": v(20, 4) * mm, "radius": 2 * mm});
            skLineSegment(sketch, "E28", {"start": v(150, 75.58) * mm, "end": v(150, -79.26) * mm, "construction": true});
            skCircle(sketch, "E29.MirrorC", {"center": v(280, 4) * mm, "radius": 2 * mm});
            skCircle(sketch, "E30", {"center": v(150, 4) * mm, "radius": 2 * mm});
            skCircle(sketch, "E31.1.0.0", {"center": v(40, 4) * mm, "radius": 2 * mm});
            skLineSegment(sketch, "E31.direction1", {"start": v(20, 4) * mm, "end": v(40, 4) * mm, "construction": true});
            skCircle(sketch, "E32.1.0.0", {"center": v(170, 4) * mm, "radius": 2 * mm});
            skLineSegment(sketch, "E32.direction1", {"start": v(150, 4) * mm, "end": v(170, 4) * mm, "construction": true});
            skCircle(sketch, "E33.1.0.0", {"center": v(260, 4) * mm, "radius": 2 * mm});
            skLineSegment(sketch, "E33.direction1", {"start": v(280, 4) * mm, "end": v(260, 4) * mm, "construction": true});
            skSolve(sketch);
        }
        {
            var Q0;
            Q0=makeQuery(id+"F4.imprint","IMPRINT",FACE,{"disambiguationData":[TD([[makeQuery(id+"F4.imprint","IMPRINT",EDGE,{"derivedFrom":sQuery(id+"F4.wireOp",EDGE,"E30")}),1.0]])]});
            var Q1;
            Q1=makeQuery(id+"F4.imprint","IMPRINT",FACE,{"disambiguationData":[TD([[makeQuery(id+"F4.imprint","IMPRINT",EDGE,{"derivedFrom":sQuery(id+"F4.wireOp",EDGE,"E29.MirrorC")}),-1.0]])]});
            var Q2;
            Q2=makeQuery(id+"F4.imprint","IMPRINT",FACE,{"disambiguationData":[TD([[makeQuery(id+"F4.imprint","IMPRINT",EDGE,{"derivedFrom":sQuery(id+"F4.wireOp",EDGE,"E27")}),1.0]])]});
            var Q3;
            Q3=makeQuery(id+"F4.imprint","IMPRINT",FACE,{"disambiguationData":[TD([[makeQuery(id+"F4.imprint","IMPRINT",EDGE,{"derivedFrom":sQuery(id+"F4.wireOp",EDGE,"E33.1.0.0")}),-1.0]])]});
            var Q4;
            Q4=makeQuery(id+"F4.imprint","IMPRINT",FACE,{"disambiguationData":[TD([[makeQuery(id+"F4.imprint","IMPRINT",EDGE,{"derivedFrom":sQuery(id+"F4.wireOp",EDGE,"E32.1.0.0")}),1.0]])]});
            var Q5;
            Q5=makeQuery(id+"F4.imprint","IMPRINT",FACE,{"disambiguationData":[TD([[makeQuery(id+"F4.imprint","IMPRINT",EDGE,{"derivedFrom":sQuery(id+"F4.wireOp",EDGE,"E31.1.0.0")}),1.0]])]});
            extrude(context, id + "F5", {"entities" : qUnion([Q0, Q1, Q2, Q3, Q4, Q5]), "operationType" : NewBodyOperationType.REMOVE, "endBound" : BoundingType.THROUGH_ALL, "oppositeDirection" : true, "depth" : 25 * mm, "offsetDistance" : 25 * mm});
        }
        {
            var Q0;
            Q0=makeQuery(id+"F5.boolean.opBoolean","COPY",FACE,{"derivedFrom":makeQuery(id+"F5.opExtrude","SWEPT_FACE",FACE,{"disambiguationData":[OSD([sQuery(id+"F4.wireOp",EDGE,"E27")])]})});
            var Q1;
            Q1=makeQuery(id+"F5.boolean.opBoolean","COPY",FACE,{"derivedFrom":makeQuery(id+"F5.opExtrude","SWEPT_FACE",FACE,{"disambiguationData":[OSD([sQuery(id+"F4.wireOp",EDGE,"E30")])]})});
            var Q2;
            Q2=makeQuery(id+"F5.boolean.opBoolean","COPY",FACE,{"derivedFrom":makeQuery(id+"F5.opExtrude","SWEPT_FACE",FACE,{"disambiguationData":[OSD([sQuery(id+"F4.wireOp",EDGE,"E29.MirrorC")])]})});
            var Q3;
            Q3=makeQuery(id+"F5.boolean.opBoolean","COPY",FACE,{"derivedFrom":makeQuery(id+"F5.opExtrude","SWEPT_FACE",FACE,{"disambiguationData":[OSD([sQuery(id+"F4.wireOp",EDGE,"E31.1.0.0")])]})});
            var Q4;
            Q4=makeQuery(id+"F5.boolean.opBoolean","COPY",FACE,{"derivedFrom":makeQuery(id+"F5.opExtrude","SWEPT_FACE",FACE,{"disambiguationData":[OSD([sQuery(id+"F4.wireOp",EDGE,"E32.1.0.0")])]})});
            var Q5;
            Q5=makeQuery(id+"F5.boolean.opBoolean","COPY",FACE,{"derivedFrom":makeQuery(id+"F5.opExtrude","SWEPT_FACE",FACE,{"disambiguationData":[OSD([sQuery(id+"F4.wireOp",EDGE,"E33.1.0.0")])]})});
            chamfer(context, id + "F6", {"entities" : qUnion([Q0, Q1, Q2, Q3, Q4, Q5]), "width" : 0.5 * mm, "tangentPropagation" : true});
        }
    });
